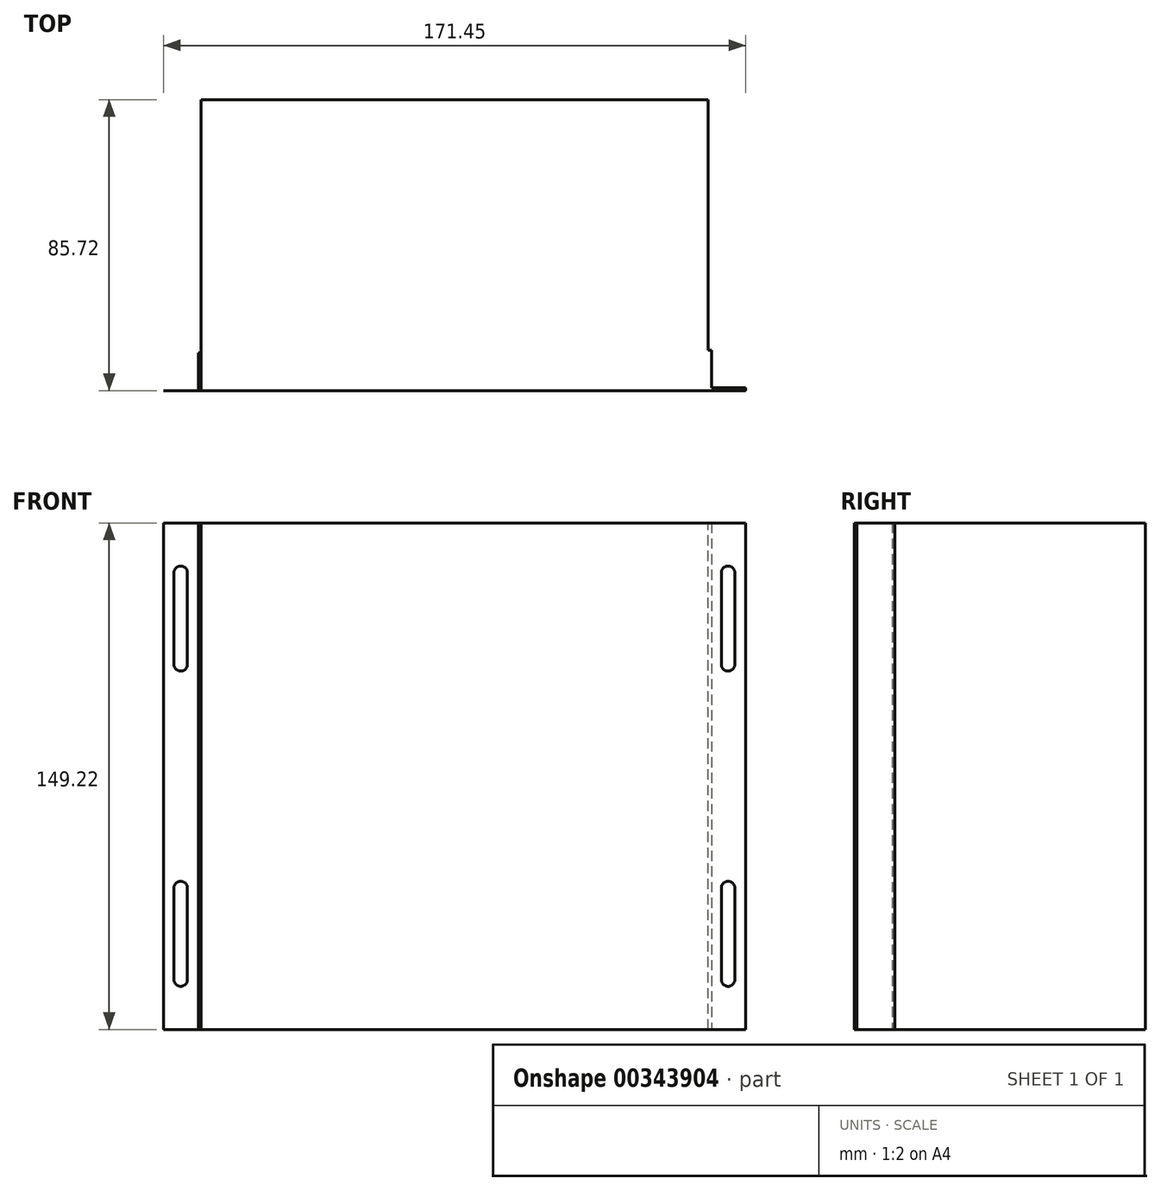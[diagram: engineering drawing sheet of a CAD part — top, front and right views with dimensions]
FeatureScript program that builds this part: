
annotation { "Feature Type Name" : "Feature", "Feature Type Description" : "" }
export const myFeature = defineFeature(function(context is Context, id is Id, definition is map)
    precondition{}
    {
        {
            var Q0;
            Q0=qCreatedBy(makeId("Front.planeOp"),FACE);
            var sketch = newSketch(context, id + "F0", { "sketchPlane" : qUnion([Q0])});
            skLineSegment(sketch, "E0.bottom", {"start": v(0, 0) * mm, "end": v(11.11, 0) * mm});
            skLineSegment(sketch, "E0.top", {"start": v(0, 149.23) * mm, "end": v(11.11, 149.23) * mm});
            skLineSegment(sketch, "E0.left", {"start": v(0, 0) * mm, "end": v(0, 149.23) * mm});
            skLineSegment(sketch, "E0.right", {"start": v(11.11, 0) * mm, "end": v(11.11, 149.23) * mm});
            skSolve(sketch);
        }
        {
            var Q0;
            Q0=qSketchRegion(id+"F0",true);
            extrude(context, id + "F1", {"entities" : qUnion([Q0]), "oppositeDirection" : true, "depth" : 1 / 812.8 * mm});
        }
        {
            var Q0;
            Q0=qCreatedBy(makeId("Front.planeOp"),FACE);
            var sketch = newSketch(context, id + "F2", { "sketchPlane" : qUnion([Q0])});
            skLineSegment(sketch, "E1.bottom", {"start": v(11.11, 149.23) * mm, "end": v(160.34, 149.23) * mm});
            skLineSegment(sketch, "E1.top", {"start": v(11.11, 0) * mm, "end": v(160.34, 0) * mm});
            skLineSegment(sketch, "E1.left", {"start": v(11.11, 149.23) * mm, "end": v(11.11, 0) * mm});
            skLineSegment(sketch, "E1.right", {"start": v(160.34, 149.23) * mm, "end": v(160.34, 0) * mm});
            skSolve(sketch);
        }
        {
            var Q0;
            Q0=qSketchRegion(id+"F2",true);
            extrude(context, id + "F3", {"entities" : qUnion([Q0]), "oppositeDirection" : true, "depth" : 85.72 * mm});
        }
        {
            var Q0;
            Q0=qCreatedBy(makeId("Front.planeOp"),FACE);
            var sketch = newSketch(context, id + "F4", { "sketchPlane" : qUnion([Q0])});
            skLineSegment(sketch, "E2.bottom", {"start": v(160.34, 0) * mm, "end": v(171.45, 0) * mm});
            skLineSegment(sketch, "E2.top", {"start": v(160.34, 149.23) * mm, "end": v(171.45, 149.23) * mm});
            skLineSegment(sketch, "E2.left", {"start": v(160.34, 0) * mm, "end": v(160.34, 149.23) * mm});
            skLineSegment(sketch, "E2.right", {"start": v(171.45, 0) * mm, "end": v(171.45, 149.23) * mm});
            skSolve(sketch);
        }
        {
            var Q0;
            Q0=makeQuery(id+"F4.imprint","IMPRINT",FACE,{"disambiguationData":[TD([[makeQuery(id+"F4.imprint","IMPRINT",EDGE,{"derivedFrom":sQuery(id+"F4.wireOp",EDGE,"E2.bottom")}),1.0]])]});
            extrude(context, id + "F5", {"entities" : qUnion([Q0]), "operationType" : NewBodyOperationType.ADD, "oppositeDirection" : true, "depth" : 0.8 * mm});
        }
        {
            var Q0;
            Q0=makeQuery(id+"F1.opExtrude","CAP_FACE",FACE,{"disambiguationData":[OSD([sQuery(id+"F0.wireOp",EDGE,"E0.bottom"),sQuery(id+"F0.wireOp",EDGE,"E0.top"),sQuery(id+"F0.wireOp",EDGE,"E0.left"),sQuery(id+"F0.wireOp",EDGE,"E0.right")])],"isStart":false});
            var sketch = newSketch(context, id + "F6", { "sketchPlane" : qUnion([Q0])});
            skLineSegment(sketch, "E3.bottom", {"start": v(-11.11, 149.23) * mm, "end": v(-5.56, 149.23) * mm});
            skLineSegment(sketch, "E3.top", {"start": v(-11.11, 0) * mm, "end": v(-5.56, 0) * mm});
            skLineSegment(sketch, "E3.left", {"start": v(-11.11, 149.23) * mm, "end": v(-11.11, 0) * mm});
            skLineSegment(sketch, "E3.right", {"start": v(-10.32, 149.23) * mm, "end": v(-10.32, 0) * mm});
            skSolve(sketch);
        }
        {
            var Q0;
            Q0=qSketchRegion(id+"F6",true);
            extrude(context, id + "F7", {"entities" : qUnion([Q0]), "depth" : 11.1 * mm});
        }
        {
            var Q0;
            Q0=makeQuery(id+"F5.opExtrude","CAP_FACE",FACE,{"disambiguationData":[OSD([sQuery(id+"F4.wireOp",EDGE,"E2.bottom"),sQuery(id+"F4.wireOp",EDGE,"E2.top"),sQuery(id+"F4.wireOp",EDGE,"E2.left"),sQuery(id+"F4.wireOp",EDGE,"E2.right")])],"isStart":false});
            var sketch = newSketch(context, id + "F8", { "sketchPlane" : qUnion([Q0])});
            skLineSegment(sketch, "E4.bottom", {"start": v(-160.34, 149.23) * mm, "end": v(-161.35, 149.23) * mm});
            skLineSegment(sketch, "E4.top", {"start": v(-160.34, 0) * mm, "end": v(-161.35, 0) * mm});
            skLineSegment(sketch, "E4.left", {"start": v(-160.34, 149.23) * mm, "end": v(-160.34, 0) * mm});
            skLineSegment(sketch, "E4.right", {"start": v(-161.35, 149.23) * mm, "end": v(-161.35, 0) * mm});
            skSolve(sketch);
        }
        {
            var Q0;
            Q0=makeQuery(id+"F8.imprint","IMPRINT",FACE,{"disambiguationData":[TD([[makeQuery(id+"F8.imprint","IMPRINT",EDGE,{"derivedFrom":sQuery(id+"F8.wireOp",EDGE,"E4.bottom")}),1.0]])]});
            extrude(context, id + "F9", {"entities" : qUnion([Q0]), "operationType" : NewBodyOperationType.ADD, "depth" : 11.1 * mm});
        }
        {
            var Q0;
            Q0=makeQuery(id+"F1.opExtrude","CAP_FACE",FACE,{"disambiguationData":[OSD([sQuery(id+"F0.wireOp",EDGE,"E0.bottom"),sQuery(id+"F0.wireOp",EDGE,"E0.top"),sQuery(id+"F0.wireOp",EDGE,"E0.left"),sQuery(id+"F0.wireOp",EDGE,"E0.right")])],"isStart":false});
            var sketch = newSketch(context, id + "F10", { "sketchPlane" : qUnion([Q0])});
            skLineSegment(sketch, "E5", {"start": v(-7.03, 134.54) * mm, "end": v(-7.03, 107.56) * mm});
            skLineSegment(sketch, "E6", {"start": v(-3.06, 134.54) * mm, "end": v(-3.06, 107.56) * mm});
            skArc(sketch, "E7", {"start": v(-7.03, 107.56) * mm, "mid": v(-5.05, 105.57) * mm, "end": v(-3.06, 107.56) * mm});
            skArc(sketch, "E8", {"start": v(-3.06, 134.54) * mm, "mid": v(-5.05, 136.53) * mm, "end": v(-7.03, 134.54) * mm});
            skLineSegment(sketch, "E9", {"start": v(-7.03, 41.67) * mm, "end": v(-7.03, 14.68) * mm});
            skLineSegment(sketch, "E10", {"start": v(-3.06, 41.67) * mm, "end": v(-3.06, 14.68) * mm});
            skArc(sketch, "E11", {"start": v(-7.03, 14.68) * mm, "mid": v(-5.05, 12.7) * mm, "end": v(-3.06, 14.68) * mm});
            skArc(sketch, "E12", {"start": v(-3.06, 41.67) * mm, "mid": v(-5.05, 43.65) * mm, "end": v(-7.03, 41.67) * mm});
            skSolve(sketch);
        }
        {
            var Q0;
            Q0=makeQuery(id+"F5.opExtrude","CAP_FACE",FACE,{"disambiguationData":[OSD([sQuery(id+"F4.wireOp",EDGE,"E2.bottom"),sQuery(id+"F4.wireOp",EDGE,"E2.top"),sQuery(id+"F4.wireOp",EDGE,"E2.left"),sQuery(id+"F4.wireOp",EDGE,"E2.right")])],"isStart":false});
            var sketch = newSketch(context, id + "F11", { "sketchPlane" : qUnion([Q0])});
            skLineSegment(sketch, "E13", {"start": v(-168.28, 134.54) * mm, "end": v(-168.28, 107.56) * mm});
            skLineSegment(sketch, "E14", {"start": v(-164.3, 134.54) * mm, "end": v(-164.3, 107.56) * mm});
            skArc(sketch, "E15", {"start": v(-168.28, 107.56) * mm, "mid": v(-166.3, 105.57) * mm, "end": v(-164.3, 107.56) * mm});
            skArc(sketch, "E16", {"start": v(-164.3, 134.54) * mm, "mid": v(-166.3, 136.53) * mm, "end": v(-168.28, 134.54) * mm});
            skLineSegment(sketch, "E17", {"start": v(-168.28, 41.67) * mm, "end": v(-168.28, 14.68) * mm});
            skLineSegment(sketch, "E18", {"start": v(-164.3, 41.67) * mm, "end": v(-164.3, 14.68) * mm});
            skArc(sketch, "E19", {"start": v(-168.28, 14.68) * mm, "mid": v(-166.3, 12.7) * mm, "end": v(-164.3, 14.68) * mm});
            skArc(sketch, "E20", {"start": v(-164.3, 41.67) * mm, "mid": v(-166.3, 43.65) * mm, "end": v(-168.28, 41.67) * mm});
            skSolve(sketch);
        }
        {
            var Q0;
            Q0=qSketchRegion(id+"F11",true);
            extrude(context, id + "F12", {"entities" : qUnion([Q0]), "operationType" : NewBodyOperationType.REMOVE, "oppositeDirection" : true, "depth" : 1.02 * mm});
        }
        {
            var Q0;
            Q0=makeQuery(id+"F10.imprint","IMPRINT",FACE,{"disambiguationData":[TD([[makeQuery(id+"F10.imprint","IMPRINT",EDGE,{"derivedFrom":sQuery(id+"F10.wireOp",EDGE,"E5")}),1.0]])]});
            var Q1;
            Q1=makeQuery(id+"F10.imprint","IMPRINT",FACE,{"disambiguationData":[TD([[makeQuery(id+"F10.imprint","IMPRINT",EDGE,{"derivedFrom":sQuery(id+"F10.wireOp",EDGE,"E9")}),1.0]])]});
            extrude(context, id + "F13", {"entities" : qUnion([Q0, Q1]), "operationType" : NewBodyOperationType.REMOVE, "oppositeDirection" : true, "depth" : 0.8 * mm});
        }
        {
            var Q0;
            Q0=makeQuery(id+"F7.opExtrude","SWEPT_BODY",BODY,{"disambiguationData":[OSD([sQuery(id+"F6.wireOp",EDGE,"E3.bottom"),sQuery(id+"F6.wireOp",EDGE,"E3.top"),sQuery(id+"F6.wireOp",EDGE,"E3.left"),sQuery(id+"F6.wireOp",EDGE,"E3.right")])]});
            var Q1;
            Q1=makeQuery(id+"F3.opExtrude","SWEPT_BODY",BODY,{"disambiguationData":[OSD([sQuery(id+"F2.wireOp",EDGE,"E1.bottom"),sQuery(id+"F2.wireOp",EDGE,"E1.top"),sQuery(id+"F2.wireOp",EDGE,"E1.left"),sQuery(id+"F2.wireOp",EDGE,"E1.right")])]});
            var Q2;
            Q2=makeQuery(id+"F1.opExtrude","SWEPT_BODY",BODY,{"disambiguationData":[OSD([sQuery(id+"F0.wireOp",EDGE,"E0.bottom"),sQuery(id+"F0.wireOp",EDGE,"E0.top"),sQuery(id+"F0.wireOp",EDGE,"E0.left"),sQuery(id+"F0.wireOp",EDGE,"E0.right")])]});
            transform(context, id + "F14", {"entities" : qUnion([Q0, Q1, Q2]), "transformType" : TransformType.TRANSLATION_3D, "dx" : 0 * mm, "dy" : 152.4 * mm, "dz" : 0 * mm, "makeCopy" : false});
        }
    });
